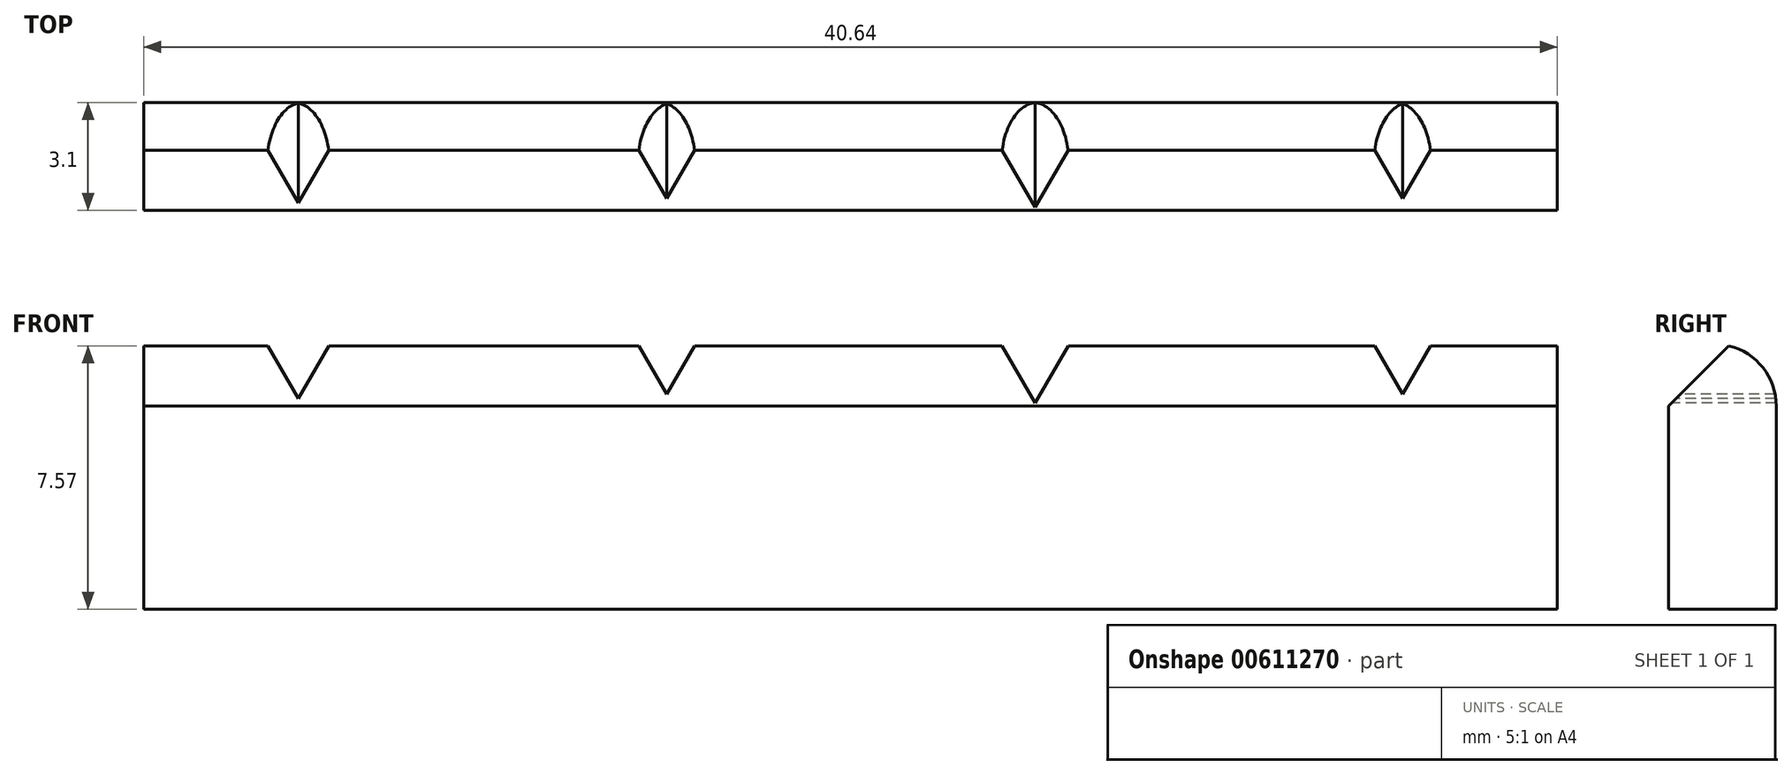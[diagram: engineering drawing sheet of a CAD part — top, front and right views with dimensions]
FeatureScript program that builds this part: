
annotation { "Feature Type Name" : "Feature", "Feature Type Description" : "" }
export const myFeature = defineFeature(function(context is Context, id is Id, definition is map)
    precondition{}
    {
        {
            var Q0;
            Q0=qCreatedBy(makeId("Top.planeOp"),FACE);
            var sketch = newSketch(context, id + "F0", { "sketchPlane" : qUnion([Q0])});
            skLineSegment(sketch, "E0.bottom", {"start": v(-20.32, 0) * mm, "end": v(20.32, 0) * mm});
            skLineSegment(sketch, "E0.top", {"start": v(-20.32, 3.1) * mm, "end": v(20.32, 3.1) * mm});
            skLineSegment(sketch, "E0.left", {"start": v(-20.32, 0) * mm, "end": v(-20.32, 3.1) * mm});
            skLineSegment(sketch, "E0.right", {"start": v(20.32, 0) * mm, "end": v(20.32, 3.1) * mm});
            skSolve(sketch);
        }
        {
            var Q0;
            Q0=makeQuery(id+"F0.imprint","IMPRINT",FACE,{"disambiguationData":[TD([[makeQuery(id+"F0.imprint","IMPRINT",EDGE,{"derivedFrom":sQuery(id+"F0.wireOp",EDGE,"E0.bottom")}),1.0]])]});
            extrude(context, id + "F1", {"entities" : qUnion([Q0]), "depth" : 7.62 * mm, "offsetDistance" : 25.4 * mm});
        }
        {
            var Q0;
            Q0=makeQuery(id+"F1.opExtrude","SWEPT_FACE",FACE,{"disambiguationData":[OSD([sQuery(id+"F0.wireOp",EDGE,"E0.bottom")])]});
            var sketch = newSketch(context, id + "F2", { "sketchPlane" : qUnion([Q0])});
            skCircle(sketch, "E1.cCircle", {"center": v(-15.87, 7.52) * mm, "radius": 0.73 * mm, "construction": true});
            skLineSegment(sketch, "E1.0", {"start": v(-14.6, 8.26) * mm, "end": v(-15.87, 6.06) * mm});
            skLineSegment(sketch, "E1.1", {"start": v(-15.87, 6.06) * mm, "end": v(-17.14, 8.26) * mm});
            skLineSegment(sketch, "E1.2", {"start": v(-17.15, 8.26) * mm, "end": v(-14.6, 8.26) * mm});
            skPoint(sketch, "E1.0.midPoint", {"position": v(-15.24, 7.16) * mm});
            skCircle(sketch, "E2.cCircle", {"center": v(-5.28, 7.65) * mm, "radius": 0.73 * mm, "construction": true});
            skLineSegment(sketch, "E2.0", {"start": v(-4.01, 8.38) * mm, "end": v(-5.28, 6.18) * mm});
            skLineSegment(sketch, "E2.1", {"start": v(-5.28, 6.18) * mm, "end": v(-6.55, 8.38) * mm});
            skLineSegment(sketch, "E2.2", {"start": v(-6.55, 8.38) * mm, "end": v(-4.01, 8.38) * mm});
            skPoint(sketch, "E2.0.midPoint", {"position": v(-4.65, 7.28) * mm});
            skCircle(sketch, "E3.cCircle", {"center": v(15.87, 7.65) * mm, "radius": 0.73 * mm, "construction": true});
            skLineSegment(sketch, "E3.0", {"start": v(17.14, 8.38) * mm, "end": v(15.87, 6.18) * mm});
            skLineSegment(sketch, "E3.1", {"start": v(15.87, 6.18) * mm, "end": v(14.6, 8.38) * mm});
            skLineSegment(sketch, "E3.2", {"start": v(14.6, 8.38) * mm, "end": v(17.14, 8.38) * mm});
            skPoint(sketch, "E3.0.midPoint", {"position": v(16.5, 7.28) * mm});
            skCircle(sketch, "E4.cCircle", {"center": v(5.3, 7.4) * mm, "radius": 0.73 * mm, "construction": true});
            skLineSegment(sketch, "E4.0", {"start": v(6.58, 8.13) * mm, "end": v(5.3, 5.93) * mm});
            skLineSegment(sketch, "E4.1", {"start": v(5.3, 5.93) * mm, "end": v(4.04, 8.13) * mm});
            skLineSegment(sketch, "E4.2", {"start": v(4.04, 8.13) * mm, "end": v(6.58, 8.13) * mm});
            skPoint(sketch, "E4.0.midPoint", {"position": v(5.94, 7.03) * mm});
            skSolve(sketch);
        }
        {
            var Q0;
            Q0=makeQuery(id+"F1.opExtrude","CAP_EDGE",EDGE,{"disambiguationData":[OSD([sQuery(id+"F0.wireOp",EDGE,"E0.top")])],"isStart":false});
            fillet(context, id + "F3", {"entities" : qUnion([Q0]), "radius" : 1.78 * mm, "tangentPropagation" : true, "allowEdgeOverflow" : false});
        }
        {
            var Q0;
            Q0=makeQuery(id+"F1.opExtrude","CAP_EDGE",EDGE,{"disambiguationData":[OSD([sQuery(id+"F0.wireOp",EDGE,"E0.bottom")])],"isStart":false});
            chamfer(context, id + "F4", {"entities" : qUnion([Q0]), "width" : 1.78 * mm, "tangentPropagation" : true});
        }
        {
            var Q0;
            {var subQ0=sQuery(id+"F2.wireOp",EDGE,"E1.1");var subQ1=sQuery(id+"F2.wireOp",EDGE,"E1.0");var subQ2=makeQuery(id+"F2.imprint","INTERSECT",VERTEX,{"derivedFrom":[subQ1,subQ0]});Q0=makeQuery(id+"F2.imprint","IMPRINT",FACE,{"disambiguationData":[TD([[makeQuery(id+"F2.imprint","IMPRINT",EDGE,{"disambiguationData":[TD([[subQ2,1.0]])],"derivedFrom":subQ1}),-1.0]])]});}
            var Q1;
            {var subQ0=sQuery(id+"F2.wireOp",EDGE,"E2.1");var subQ1=sQuery(id+"F2.wireOp",EDGE,"E2.0");var subQ2=makeQuery(id+"F2.imprint","INTERSECT",VERTEX,{"derivedFrom":[subQ1,subQ0]});Q1=makeQuery(id+"F2.imprint","IMPRINT",FACE,{"disambiguationData":[TD([[makeQuery(id+"F2.imprint","IMPRINT",EDGE,{"disambiguationData":[TD([[subQ2,1.0]])],"derivedFrom":subQ1}),-1.0]])]});}
            var Q2;
            {var subQ0=sQuery(id+"F2.wireOp",EDGE,"E4.1");var subQ1=sQuery(id+"F2.wireOp",EDGE,"E4.0");var subQ2=makeQuery(id+"F2.imprint","INTERSECT",VERTEX,{"derivedFrom":[subQ1,subQ0]});Q2=makeQuery(id+"F2.imprint","IMPRINT",FACE,{"disambiguationData":[TD([[makeQuery(id+"F2.imprint","IMPRINT",EDGE,{"disambiguationData":[TD([[subQ2,1.0]])],"derivedFrom":subQ1}),-1.0]])]});}
            var Q3;
            {var subQ0=sQuery(id+"F2.wireOp",EDGE,"E3.1");var subQ1=sQuery(id+"F2.wireOp",EDGE,"E3.0");var subQ2=makeQuery(id+"F2.imprint","INTERSECT",VERTEX,{"derivedFrom":[subQ1,subQ0]});Q3=makeQuery(id+"F2.imprint","IMPRINT",FACE,{"disambiguationData":[TD([[makeQuery(id+"F2.imprint","IMPRINT",EDGE,{"disambiguationData":[TD([[subQ2,1.0]])],"derivedFrom":subQ1}),-1.0]])]});}
            extrude(context, id + "F5", {"entities" : qUnion([Q0, Q1, Q2, Q3]), "operationType" : NewBodyOperationType.REMOVE, "oppositeDirection" : true, "depth" : 25.4 * mm, "offsetDistance" : 25.4 * mm});
        }
    });
